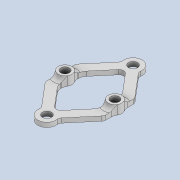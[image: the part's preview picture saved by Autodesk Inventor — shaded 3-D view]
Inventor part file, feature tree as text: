
AUTODESK INVENTOR PART (.ipt)
format: ipt  version: 2020 (Build 240168000, 168)  size: 299,520 bytes
history: native  units: mm
features: sketch x4, fillet x3, projected_geometry x3, extrude x2, hole x2
ambient origin geometry x8: Origin, YZ Plane, XZ Plane, XY Plane, X Axis, Y Axis, Z Axis, Center Point
bodies: Solid1 (feature_tree)
feature tree (14):
  extrude  "Extrusion1"  Depth=19.0mm
  hole  "Hole1"  [1 undecoded]
  hole  "Hole2"  [1 undecoded]
  extrude  "Extrusion2"  Depth=2.0mm
  fillet  "Fillet1"  Radius=2.0mm
  fillet  "Fillet2"  Radius=1.0mm
  fillet  "Fillet3"  Radius=1.0mm
  sketch  "Sketch1"  dims[d0=19.0mm d1=5.5mm]
  sketch  "Sketch2"  dims[d2=5.5mm d3=3.0mm]
  projected_geometry  "Projected Loop1"
  sketch  "Sketch3"  dims[d4=2.0mm d5=3.0mm]
  projected_geometry  "Projected Loop2"
  sketch  "Sketch4"  dims[d6=2.0mm d7=2.0mm d8=2.0mm d9=1.0mm d10=1.0mm d11=4.0mm d12=3.0mm d13=3.0mm d14=4.0mm d15=1.0mm d16=0.0mm d17=1.9mm d18=6.0mm d19=4.0mm d20=2.0mm d21=90.0deg d22=100.0mm d23=0.0mm d24=2.0mm d25=6.0mm d26=4.0mm d27=2.0mm d28=90.0deg d29=100.0mm d30=0.0mm d31=3.0mm d32=3.0mm d33=1.0mm d34=0.0mm d35=2.0mm d36=1.0mm d37=1.0mm]
  projected_geometry  "Projected Loop3"
note: 2 required parameter values undecoded (feature->parameter linkage not recoverable at this tier; creation-order binding heuristic only, values carry confidence <= 0.55)
